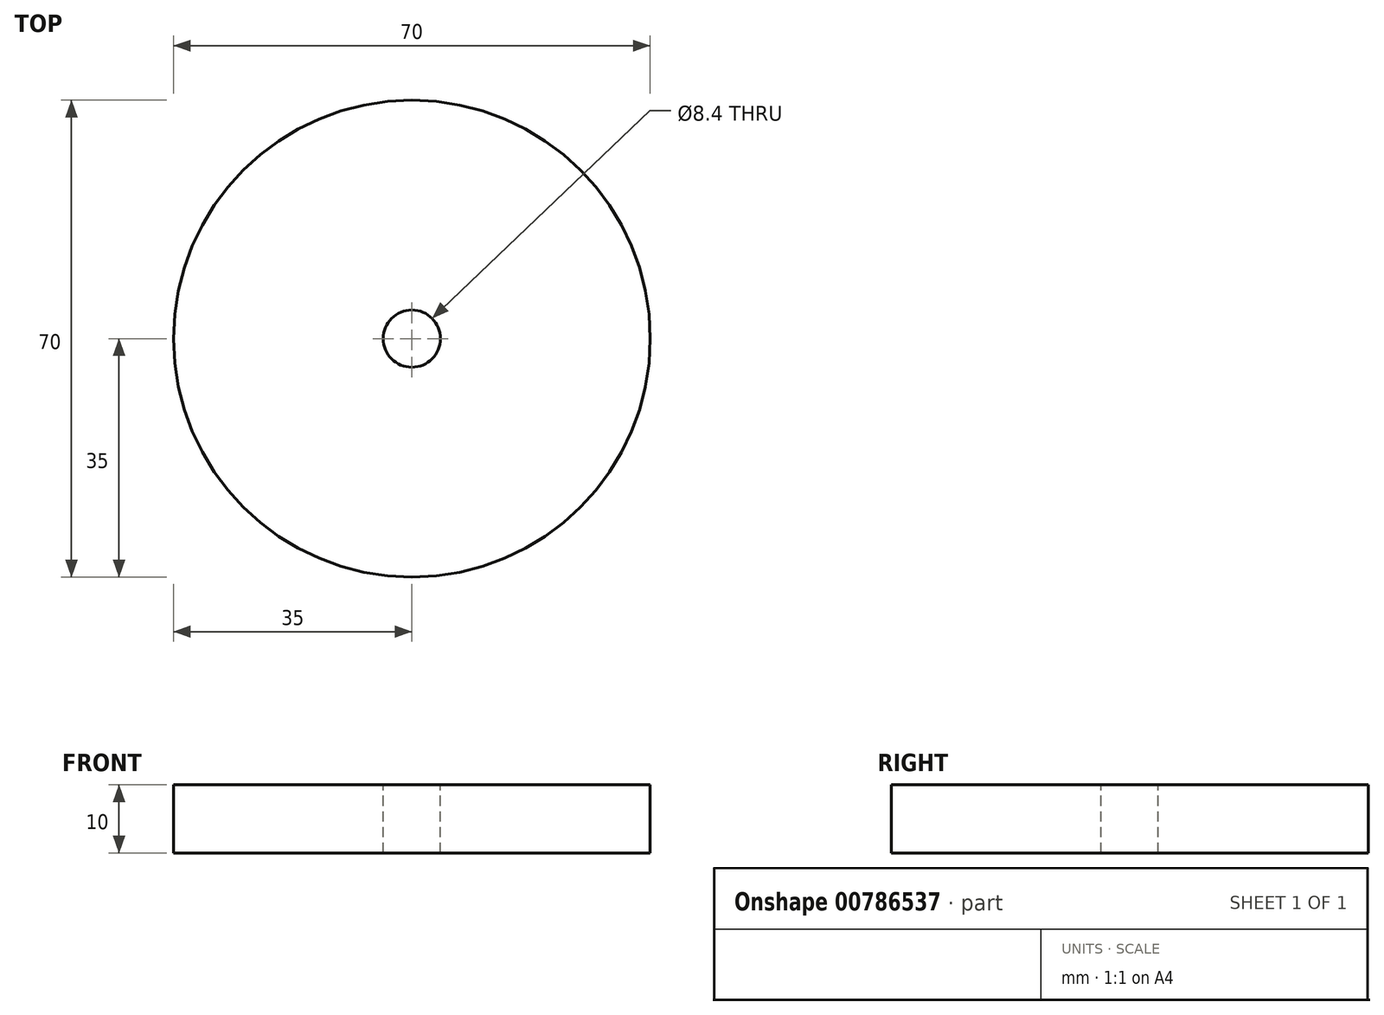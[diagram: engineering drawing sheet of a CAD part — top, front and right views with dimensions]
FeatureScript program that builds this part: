
annotation { "Feature Type Name" : "Feature", "Feature Type Description" : "" }
export const myFeature = defineFeature(function(context is Context, id is Id, definition is map)
    precondition{}
    {
        {
            var Q0;
            Q0=qCreatedBy(makeId("Top.planeOp"),FACE);
            var sketch = newSketch(context, id + "F0", { "sketchPlane" : qUnion([Q0])});
            skCircle(sketch, "E0", {"center": v(0, 0) * mm, "radius": 35 * mm});
            skCircle(sketch, "E1", {"center": v(0, 0) * mm, "radius": 4.2 * mm});
            skSolve(sketch);
        }
        {
            var Q0;
            Q0 = qSketchRegion(id + "F0", true);
            extrude(context, id + "F1", {"entities" : qUnion([Q0]), "oppositeDirection" : true, "depth" : 10 * mm, "offsetDistance" : 25 * mm});
        }
    });
